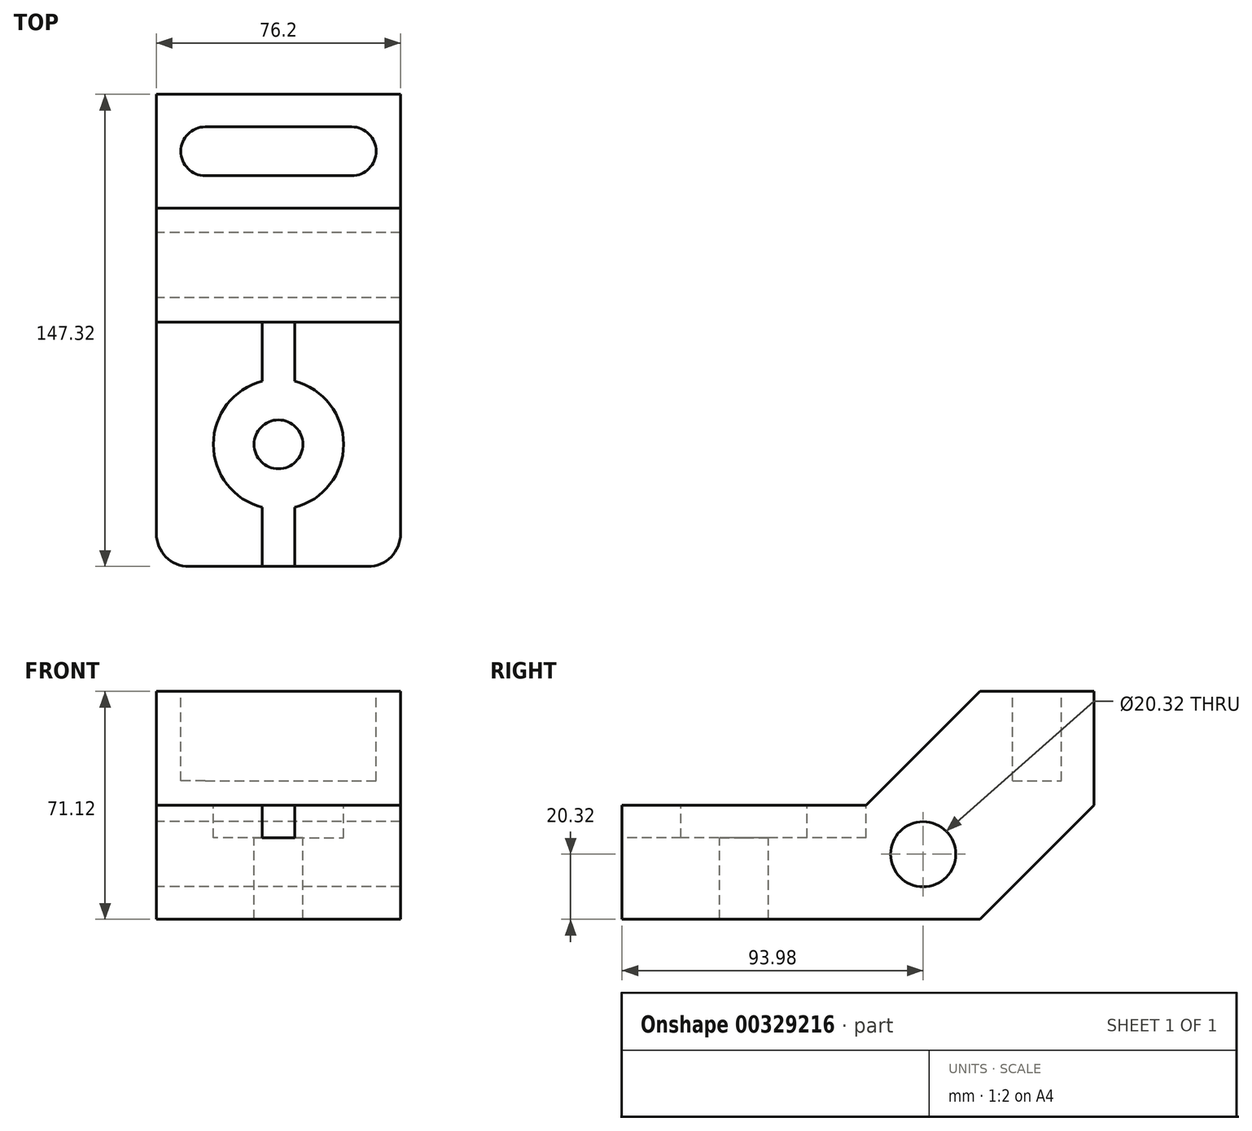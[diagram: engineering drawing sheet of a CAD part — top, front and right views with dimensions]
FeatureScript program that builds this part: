
annotation { "Feature Type Name" : "Feature", "Feature Type Description" : "" }
export const myFeature = defineFeature(function(context is Context, id is Id, definition is map)
    precondition{}
    {
        {
            var Q0;
            Q0=qCreatedBy(makeId("Right.planeOp"),FACE);
            var sketch = newSketch(context, id + "F0", { "sketchPlane" : qUnion([Q0])});
            skLineSegment(sketch, "E0", {"start": v(0, 0) * mm, "end": v(111.76, 0) * mm});
            skLineSegment(sketch, "E1", {"start": v(111.76, 0) * mm, "end": v(147.32, 35.56) * mm});
            skLineSegment(sketch, "E2", {"start": v(147.32, 35.56) * mm, "end": v(147.32, 71.12) * mm});
            skLineSegment(sketch, "E3", {"start": v(147.32, 71.12) * mm, "end": v(111.76, 71.12) * mm});
            skLineSegment(sketch, "E4", {"start": v(111.76, 71.12) * mm, "end": v(76.2, 35.56) * mm});
            skLineSegment(sketch, "E5", {"start": v(76.2, 35.56) * mm, "end": v(0, 35.56) * mm});
            skLineSegment(sketch, "E6", {"start": v(0, 35.56) * mm, "end": v(0, 0) * mm});
            skCircle(sketch, "E7", {"center": v(93.98, 20.32) * mm, "radius": 10.16 * mm});
            skSolve(sketch);
        }
        {
            var Q0;
            Q0=makeQuery(id+"F0.imprint","IMPRINT",FACE,{"disambiguationData":[TD([[makeQuery(id+"F0.imprint","IMPRINT",EDGE,{"derivedFrom":sQuery(id+"F0.wireOp",EDGE,"E0")}),1.0]])]});
            extrude(context, id + "F1", {"entities" : qUnion([Q0]), "depth" : 76.2 * mm});
        }
        {
            var Q0;
            Q0=makeQuery(id+"F1.opExtrude","CAP_EDGE",EDGE,{"disambiguationData":[OSD([sQuery(id+"F0.wireOp",EDGE,"E6")])],"isStart":false});
            var Q1;
            Q1=makeQuery(id+"F1.opExtrude","CAP_EDGE",EDGE,{"disambiguationData":[OSD([sQuery(id+"F0.wireOp",EDGE,"E6")])],"isStart":true});
            fillet(context, id + "F2", {"entities" : qUnion([Q0, Q1]), "radius" : 10.16 * mm, "tangentPropagation" : true, "allowEdgeOverflow" : false});
        }
        {
            var Q0;
            Q0=makeQuery(id+"F1.opExtrude","SWEPT_FACE",FACE,{"disambiguationData":[OSD([sQuery(id+"F0.wireOp",EDGE,"E3")])]});
            var sketch = newSketch(context, id + "F3", { "sketchPlane" : qUnion([Q0])});
            skLineSegment(sketch, "E8", {"start": v(15.24, 137.16) * mm, "end": v(60.96, 137.16) * mm});
            skLineSegment(sketch, "E9", {"start": v(15.24, 121.92) * mm, "end": v(60.96, 121.92) * mm});
            skArc(sketch, "E10", {"start": v(60.96, 121.92) * mm, "mid": v(68.58, 129.54) * mm, "end": v(60.96, 137.16) * mm});
            skArc(sketch, "E11", {"start": v(15.24, 137.16) * mm, "mid": v(7.62, 129.54) * mm, "end": v(15.24, 121.92) * mm});
            skSolve(sketch);
        }
        {
            var Q0;
            Q0=makeQuery(id+"F3.imprint","IMPRINT",FACE,{"disambiguationData":[TD([[makeQuery(id+"F3.imprint","IMPRINT",EDGE,{"derivedFrom":sQuery(id+"F3.wireOp",EDGE,"E8")}),-1.0]])]});
            extrude(context, id + "F4", {"entities" : qUnion([Q0]), "operationType" : NewBodyOperationType.REMOVE, "oppositeDirection" : true, "depth" : 27.94 * mm});
        }
        {
            var Q0;
            Q0=makeQuery(id+"F1.opExtrude","SWEPT_FACE",FACE,{"disambiguationData":[OSD([sQuery(id+"F0.wireOp",EDGE,"E5")])]});
            var sketch = newSketch(context, id + "F5", { "sketchPlane" : qUnion([Q0])});
            skLineSegment(sketch, "E12", {"start": v(33.02, 76.2) * mm, "end": v(33.02, 0) * mm});
            skLineSegment(sketch, "E13", {"start": v(33.02, 0) * mm, "end": v(43.18, 0) * mm});
            skLineSegment(sketch, "E14", {"start": v(43.18, 0) * mm, "end": v(43.18, 76.2) * mm});
            skLineSegment(sketch, "E15", {"start": v(33.02, 76.2) * mm, "end": v(43.18, 76.2) * mm});
            skPoint(sketch, "E16", {"position": v(38.1, 38.1) * mm});
            skSolve(sketch);
        }
        {
            var Q0;
            Q0=makeQuery(id+"F5.imprint","IMPRINT",FACE,{"disambiguationData":[TD([[makeQuery(id+"F5.imprint","IMPRINT",EDGE,{"derivedFrom":sQuery(id+"F5.wireOp",EDGE,"E12")}),1.0]])]});
            extrude(context, id + "F6", {"entities" : qUnion([Q0]), "operationType" : NewBodyOperationType.REMOVE, "oppositeDirection" : true, "depth" : 10.16 * mm});
        }
        {
            var Q0;
            Q0=sQuery(id+"F5.wireOp",VERTEX,"E16");
            var Q1;
            Q1=makeQuery(id+"F1.opExtrude","SWEPT_BODY",BODY,{"disambiguationData":[OSD([sQuery(id+"F0.wireOp",EDGE,"E0"),sQuery(id+"F0.wireOp",EDGE,"E1"),sQuery(id+"F0.wireOp",EDGE,"E2"),sQuery(id+"F0.wireOp",EDGE,"E3"),sQuery(id+"F0.wireOp",EDGE,"E4"),sQuery(id+"F0.wireOp",EDGE,"E5"),sQuery(id+"F0.wireOp",EDGE,"E6"),sQuery(id+"F0.wireOp",EDGE,"E7")])]});
            hole(context, id + "F7", {"style" : HoleStyle.C_BORE, "endStyle" : HoleEndStyle.THROUGH, "holeDiameter" : 15.24 * mm, "cBoreDiameter" : 40.64 * mm, "cBoreDepth" : 0 * mm, "tappedDepth" : 12.7 * mm, "tapClearance" : 3, "locations" : qUnion([Q0]), "scope" : qUnion([Q1])});
        }
    });
